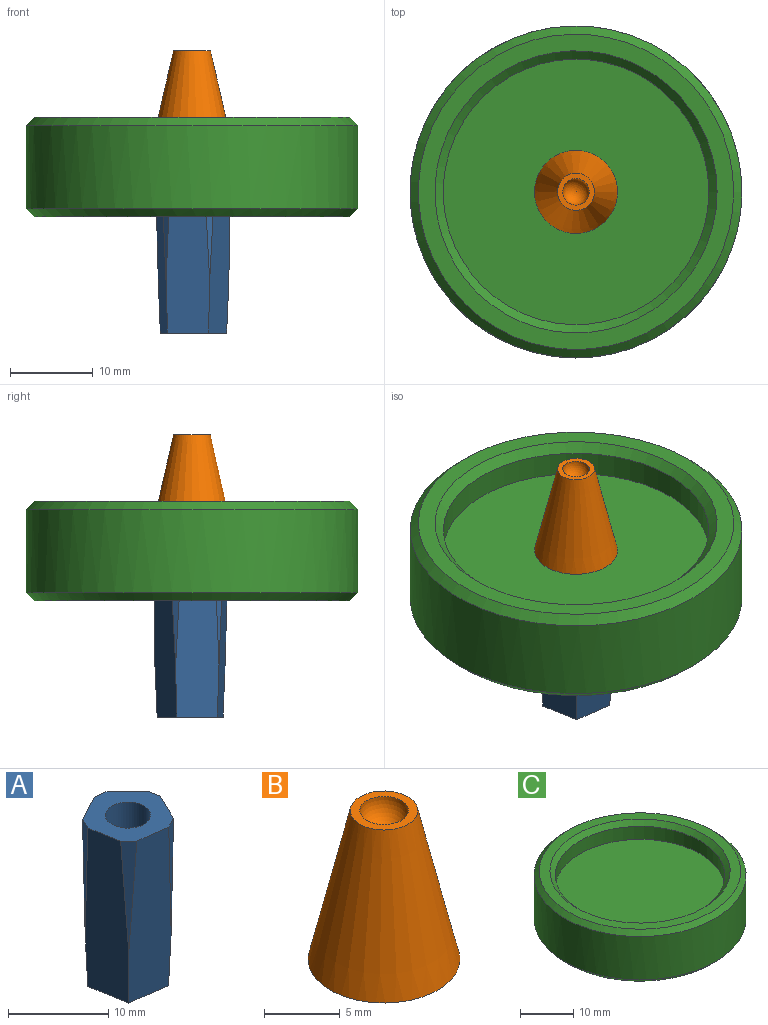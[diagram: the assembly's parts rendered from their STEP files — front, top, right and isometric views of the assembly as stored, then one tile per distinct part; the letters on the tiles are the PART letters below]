
ASSEMBLY  parts=3 mates=2
PART A: 13 faces, bbox 9x8.9x20 mm
  f0: plane 20x4.68mm, normal (-0.47,0.88,-0.03), area 96.3mm2, adj f1,f4,f6,f7,f8,f9
  f1: plane 20x5.23mm, normal (-0.98,-0.18,-0.03), area 96.3mm2, adj f0,f2,f6,f7,f8,f10
  f2: plane 20x5.26mm, normal (-0.14,-0.99,-0.03), area 96.3mm2, adj f1,f3,f6,f7,f10,f12
  f3: plane 20x4.78mm, normal (0.9,-0.44,-0.03), area 96.3mm2, adj f2,f4,f6,f7,f11,f12
  f4: plane 20x3.86mm, normal (0.69,0.72,-0.03), area 96.3mm2, adj f0,f3,f6,f7,f9,f11
  f5: cylinder r=2.25mm len=20mm, axis (0,0,1), area 282.7mm2, adj f6,f7
  f6: plane 7.99x7.94mm, normal (0,0,-1), area 26.9mm2, adj f0,f1,f2,f3,f4,f5
  f7: plane 9x8.95mm, normal (0,0,1), area 43.7mm2, adj f0,f1,f2,f3,f4,f5,f8,f9
  f8: plane 13.62x1.46mm, normal (-0.9,0.44,0), area 11mm2, adj f0,f1,f7
  f9: plane 13.62x1.6mm, normal (0.14,0.99,0), area 11mm2, adj f0,f4,f7
  f10: plane 13.62x1.17mm, normal (-0.69,-0.72,0), area 11mm2, adj f1,f2,f7
  f11: plane 13.62x1.59mm, normal (0.98,0.18,0), area 11mm2, adj f3,f4,f7
  f12: plane 13.62x1.43mm, normal (0.47,-0.88,0), area 11mm2, adj f2,f3,f7
PART B: 4 faces, bbox 10x10x12 mm
  f0: cone r=5mm half-angle=13deg, axis (0,0,-1), area 279.7mm2, adj f1,f2
  f1: plane 4.46x4.46mm, normal (0,0,1), area 7.6mm2, adj f0,f3
  f2: plane 10x10mm, normal (0,0,-1), area 78.5mm2, adj f0
  f3: sphere r=1.6mm, area 16.1mm2, adj f1
PART C: 11 faces, bbox 40x40x12 mm
  f0: plane 38x38mm, normal (0,0,1), area 226.2mm2, adj f9,f10
  f1: cylinder r=20mm len=40mm, axis (0,0,1), area 1256.6mm2, adj f8,f9
  f2: plane 38x38mm, normal (0,0,-1), area 226.2mm2, adj f7,f8
  f3: cylinder r=16mm len=32mm, axis (0,0,1), area 502.7mm2, adj f4,f7
  f4: plane 32x32mm, normal (0,0,-1), area 804.2mm2, adj f3
  f5: plane 32x32mm, normal (0,0,1), area 804.2mm2, adj f6
  f6: cylinder r=16mm len=32mm, axis (0,0,1), area 301.6mm2, adj f5,f10
  f7: cone r=17mm half-angle=45deg, axis (0,0,-1), area 146.6mm2, adj f2,f3
  f8: cone r=20mm half-angle=45deg, axis (0,0,1), area 173.3mm2, adj f1,f2
  f9: cone r=19mm half-angle=45deg, axis (0,0,-1), area 173.3mm2, adj f0,f1
  f10: cone r=16mm half-angle=45deg, axis (0,0,1), area 146.6mm2, adj f0,f6
PLACE A t=(0,0,1)mm
PLACE B t=(0,0,3)mm
PLACE C t=(0,0,2.82)mm
MATE fastened C.f1 <-> A.f5  axis (0,0,-1) through (0,0,1)mm
MATE fastened B.f0 <-> C.f1  axis (0,0,-1) through (0,0,3)mm
